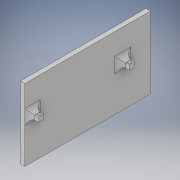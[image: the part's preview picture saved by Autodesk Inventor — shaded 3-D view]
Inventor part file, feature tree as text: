
AUTODESK INVENTOR PART (.ipt)
format: ipt  version: 2019 (Build 230136000, 136)  size: 184,320 bytes
history: native  units: in
note: dims shown in document units (in); Inventor stores cm internally (conversion verified against a paired STEP export)
features: sketch x4, extrude x3, projected_geometry x2, other x1, hole x1, fillet x1
ambient origin geometry x8: Origin, YZ Plane, XZ Plane, XY Plane, X Axis, Y Axis, Z Axis, Center Point
bodies: Solid1 (feature_tree)
feature tree (12):
  other  "wire gaurd"
  extrude  "Extrusion1"  Depth=7.0in
  extrude  "Extrusion2"  Depth=1.5in
  hole  "Hole1"  [1 undecoded]
  extrude  "Extrusion4"  Depth=0.3in TaperAngle=0.0deg
  fillet  "Fillet1"  Radius=5.039in
  sketch  "Sketch1"  dims[d0=4.0in d1=7.0in]
  sketch  "Sketch2"  dims[d2=0.25in d3=0.0in d4=1.5in]
  sketch  "Sketch3"  dims[d5=1.5in d6=0.25in]
  projected_geometry  "Projected Loop1"
  projected_geometry  "Projected Loop2"
  sketch  "Sketch4"  dims[d7=0.25in d8=0.5in d9=0.0in d10=5.039in d11=5.05in d12=0.3in d13=0.3in d15=0.15in d16=0.5in d17=0.3in d20=0.1875in d21=0.75in d22=0.375in d23=0.25in d24=0.5635in d25=1.0in d26=0.8108in d28=0.125in d29=0.125in d30=0.25in d33=0.125in d34=0.0in d35=0.3in]
note: 1 required parameter value undecoded (feature->parameter linkage not recoverable at this tier; creation-order binding heuristic only, values carry confidence <= 0.55)
